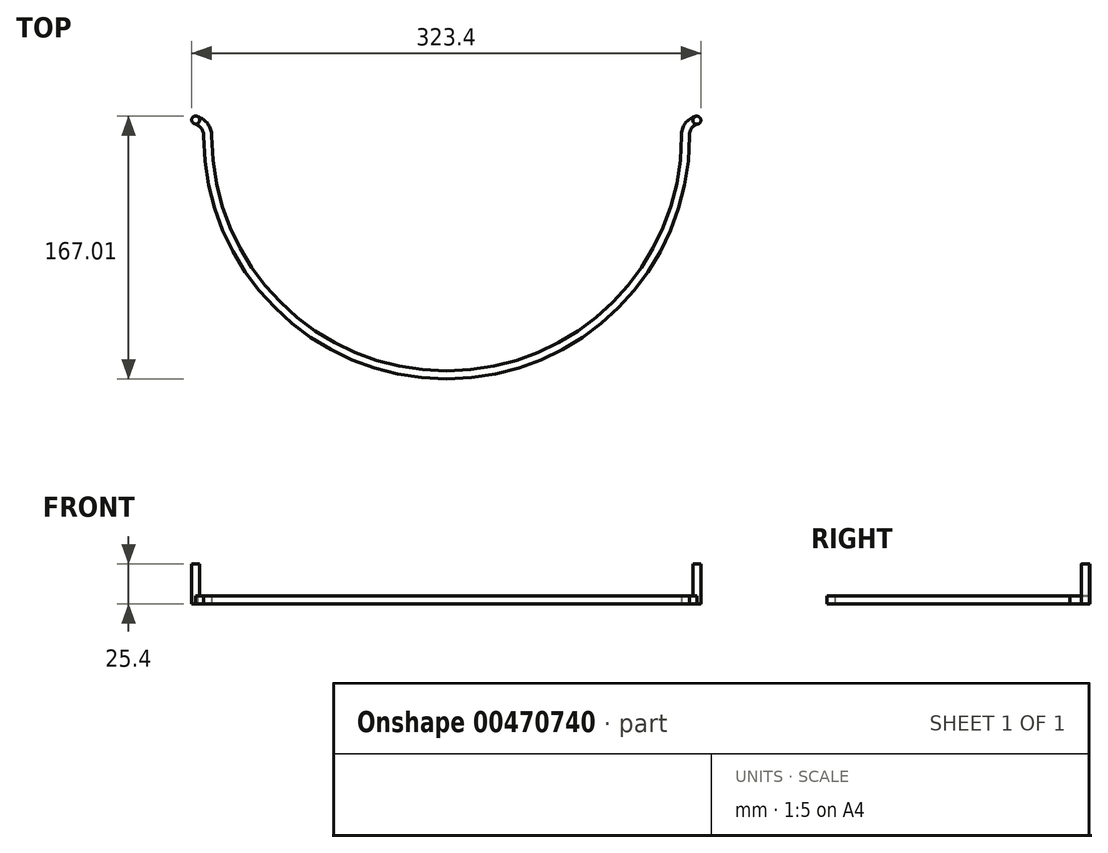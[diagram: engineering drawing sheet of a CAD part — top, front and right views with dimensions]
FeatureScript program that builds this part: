
annotation { "Feature Type Name" : "Feature", "Feature Type Description" : "" }
export const myFeature = defineFeature(function(context is Context, id is Id, definition is map)
    precondition{}
    {
        {
            var Q0;
            Q0=qCreatedBy(makeId("Top.planeOp"),FACE);
            var sketch = newSketch(context, id + "F0", { "sketchPlane" : qUnion([Q0])});
            skArc(sketch, "E0", {"start": v(-298.45, 0) * mm, "mid": v(-149.23, -149.23) * mm, "end": v(0, 0) * mm});
            skLineSegment(sketch, "E1", {"start": v(-298.45, 0) * mm, "end": v(-303.53, 0) * mm});
            skLineSegment(sketch, "E2", {"start": v(0, 0) * mm, "end": v(5.08, 0) * mm});
            skArc(sketch, "E3", {"start": v(-303.53, 0) * mm, "mid": v(-149.23, -154.3) * mm, "end": v(5.08, 0) * mm});
            skArc(sketch, "E4", {"start": v(-303.53, 0) * mm, "mid": v(-304.92, 4.58) * mm, "end": v(-308.61, 7.62) * mm});
            skArc(sketch, "E5", {"start": v(-298.45, 0) * mm, "mid": v(-301.3, 8.13) * mm, "end": v(-308.61, 12.7) * mm});
            skLineSegment(sketch, "E6", {"start": v(-308.61, 12.7) * mm, "end": v(-308.61, 7.62) * mm});
            skCircle(sketch, "E7", {"center": v(-308.61, 10.16) * mm, "radius": 2.54 * mm});
            skArc(sketch, "E8", {"start": v(10.16, 7.62) * mm, "mid": v(6.21, 4.75) * mm, "end": v(5.08, 0) * mm});
            skArc(sketch, "E9", {"start": v(10.16, 12.7) * mm, "mid": v(2.57, 8.36) * mm, "end": v(0, 0) * mm});
            skLineSegment(sketch, "E10", {"start": v(10.16, 12.7) * mm, "end": v(10.16, 7.62) * mm});
            skCircle(sketch, "E11", {"center": v(10.16, 10.16) * mm, "radius": 2.54 * mm});
            skSolve(sketch);
        }
        {
            var Q0;
            Q0=makeQuery(id+"F0.imprint","IMPRINT",FACE,{"disambiguationData":[TD([[makeQuery(id+"F0.imprint","IMPRINT",EDGE,{"derivedFrom":sQuery(id+"F0.wireOp",EDGE,"E0")}),-1.0]])]});
            var Q1;
            Q1=makeQuery(id+"F0.imprint","IMPRINT",FACE,{"disambiguationData":[TD([[makeQuery(id+"F0.imprint","IMPRINT",EDGE,{"derivedFrom":sQuery(id+"F0.wireOp",EDGE,"E1")}),-1.0]])]});
            var Q2;
            {var subQ0=sQuery(id+"F0.wireOp",EDGE,"E2");Q2=makeQuery(id+"F0.imprint","IMPRINT",FACE,{"disambiguationData":[TD([[makeQuery(id+"F0.imprint","IMPRINT",EDGE,{"derivedFrom":subQ0}),1.0]])]});}
            extrude(context, id + "F1", {"entities" : qUnion([Q0, Q1, Q2]), "depth" : 5.08 * mm});
        }
        {
            var Q0;
            Q0=qCreatedBy(makeId("Top.planeOp"),FACE);
            var sketch = newSketch(context, id + "F2", { "sketchPlane" : qUnion([Q0])});
            skCircle(sketch, "E12", {"center": v(-308.61, 10.16) * mm, "radius": 2.54 * mm});
            skCircle(sketch, "E13", {"center": v(9.7, 10.01) * mm, "radius": 2.54 * mm});
            skSolve(sketch);
        }
        {
            var Q0;
            Q0=makeQuery(id+"F2.imprint","IMPRINT",FACE,{"disambiguationData":[TD([[makeQuery(id+"F2.imprint","IMPRINT",EDGE,{"derivedFrom":sQuery(id+"F2.wireOp",EDGE,"E13")}),1.0]])]});
            var Q1;
            Q1=makeQuery(id+"F2.imprint","IMPRINT",FACE,{"disambiguationData":[TD([[makeQuery(id+"F2.imprint","IMPRINT",EDGE,{"derivedFrom":sQuery(id+"F2.wireOp",EDGE,"E12")}),1.0]])]});
            extrude(context, id + "F3", {"entities" : qUnion([Q0, Q1]), "operationType" : NewBodyOperationType.ADD, "depth" : 25.4 * mm, "hasSecondDirection" : true, "secondDirectionOppositeDirection" : true, "secondDirectionDepth" : 0 * mm});
        }
    });
